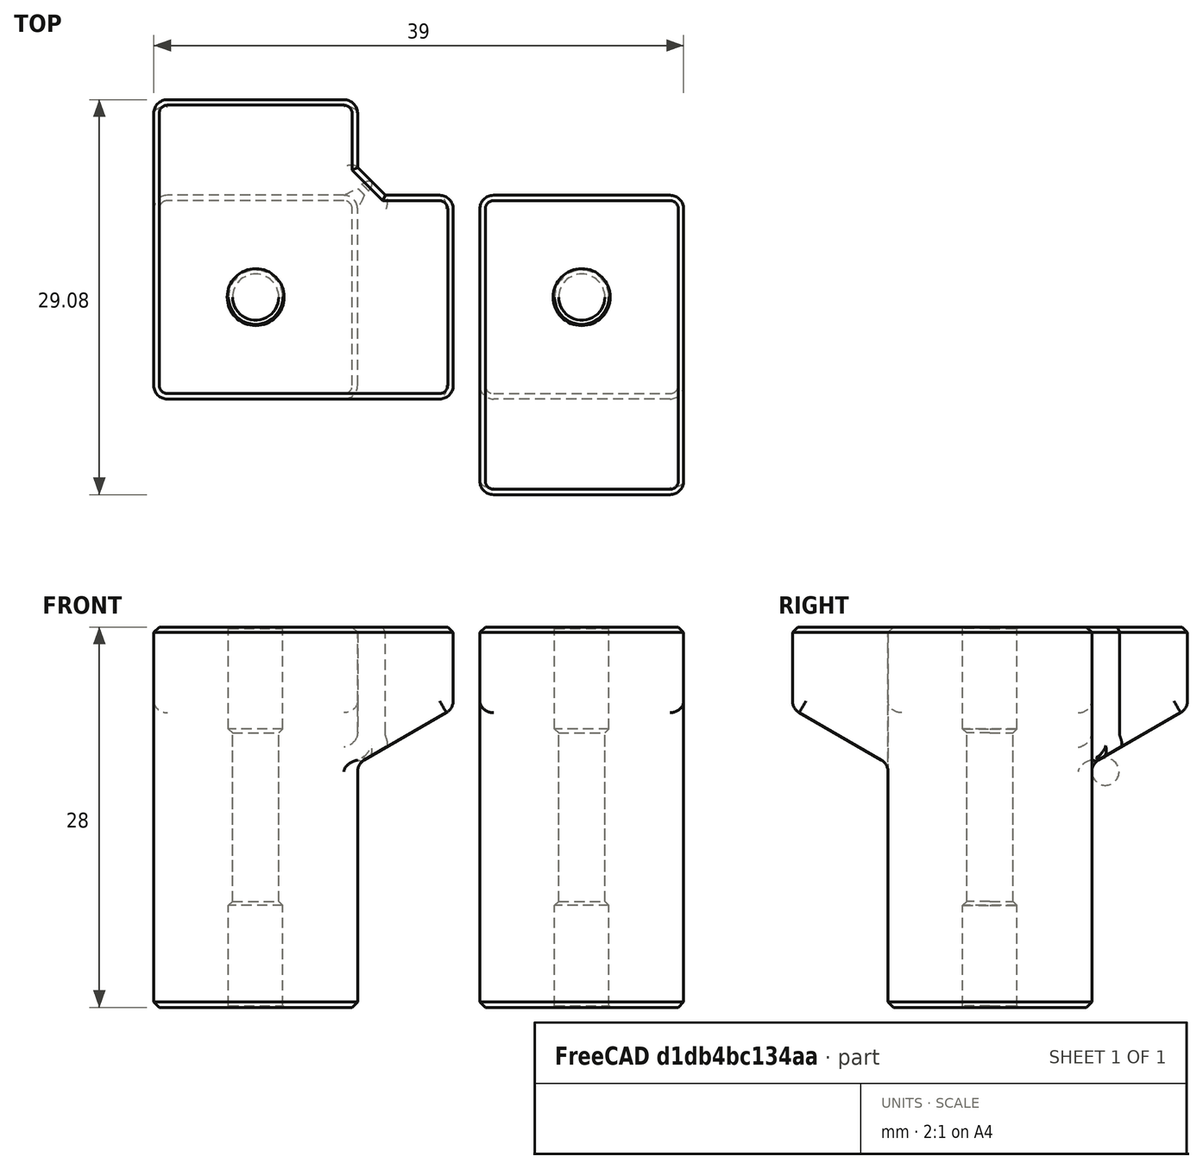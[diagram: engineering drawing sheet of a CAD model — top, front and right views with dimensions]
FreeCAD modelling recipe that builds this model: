
FCSTD DOCUMENT  (FreeCAD 0.18R16146 (Git))
Label: foot-extend
License: All rights reserved
LicenseURL: http://en.wikipedia.org/wiki/All_rights_reserved
objects: Part::Feature×7, Part::Cylinder×4, Part::MultiFuse×3, Part::MultiCommon×2, Part::Chamfer×2, Part::Cut×2
note: 20 computed .brp shape members not serialized (recipe doc carries the construction recipe); baked Part::Feature solids carry a one-line shape summary decoded from their .brp

FEATURE [Part::Feature] Part__Feature1068001  label="v0 foot_skirt_left004"
  Placement = pos=(0,-0.35,28) rot=(0,0,1;0rad)
  shape: bbox 22.04 x 22.04 x 23 mm, 63 faces (baked)
FEATURE [Part::Feature] Part__Feature1071001  label="v0 foot_skirt_left005"
  Placement = pos=(-0.5,0.15,28) rot=(0,0,1;0rad)
  shape: bbox 15 x 22.04 x 23 mm, 41 faces (baked)
FEATURE [Part::Feature] Part__Feature1071002  label="v0 foot_skirt_left006"
  Placement = pos=(-0.5,0.15,23) rot=(0,0,1;0rad)
  shape: bbox 15 x 22.04 x 23 mm, 41 faces (baked)
FEATURE [Part::Feature] Part__Feature1071003  label="v0 foot_skirt_left007"
  Placement = pos=(0,-0.35,23) rot=(0,0,1;0rad)
  shape: bbox 22.04 x 22.04 x 23 mm, 63 faces (baked)
FEATURE [Part::Cylinder] Cylinder
  Angle = 360
  AttacherType = Attacher::AttachEngine3D
  Height = 10
  Radius = 16
FEATURE [Part::Cylinder] Cylinder001
  Angle = 360
  AttacherType = Attacher::AttachEngine3D
  Height = 10
  Radius = 16
FEATURE [Part::MultiCommon] Common
  Shapes = -> [Cylinder,Part__Feature1071003]
FEATURE [Part::MultiCommon] Common001
  Shapes = -> [Cylinder001,Part__Feature1071002]
FEATURE [Part::MultiFuse] Fusion
  Shapes = -> [Part__Feature1071001,Common]
FEATURE [Part::MultiFuse] Fusion001
  Shapes = -> [Part__Feature1068001,Common001]
FEATURE [Part::Cylinder] Cylinder002
  Angle = 360
  AttacherType = Attacher::AttachEngine3D
  Height = 8
  Radius = 2
FEATURE [Part::Cylinder] Cylinder003
  Angle = 360
  AttacherType = Attacher::AttachEngine3D
  Height = 8
  Placement = pos=(0,0,20) rot=(0,0,1;0rad)
  Radius = 2
FEATURE [Part::Chamfer] Chamfer
  Base = -> Cylinder002
  Edges = 1 edges r=0.5: [Edge1]
FEATURE [Part::Chamfer] Chamfer001
  Base = -> Cylinder003
  Edges = 1 edges r=0.5: [Edge3]
FEATURE [Part::MultiFuse] Fusion002
  Shapes = -> [Chamfer,Chamfer001]
FEATURE [Part::Feature] Fusion002001  label="Fusion003"
  shape: bbox 4 x 4 x 28 mm, 8 faces, 2 solids (baked)
FEATURE [Part::Cut] Cut
  Base = -> Fusion001
  Tool = -> Fusion002001
FEATURE [Part::Cut] Cut001
  Base = -> Fusion
  Placement = pos=(24,0,0) rot=(0,0,1;0rad)
  Tool = -> Fusion002
FEATURE [Part::Feature] Cut001001  label="Cut002"
  shape: bbox 15 x 22.04 x 28 mm, 45 faces (baked)
FEATURE [Part::Feature] Cut001002  label="Cut003"
  shape: bbox 22.04 x 22.04 x 28 mm, 67 faces (baked)
